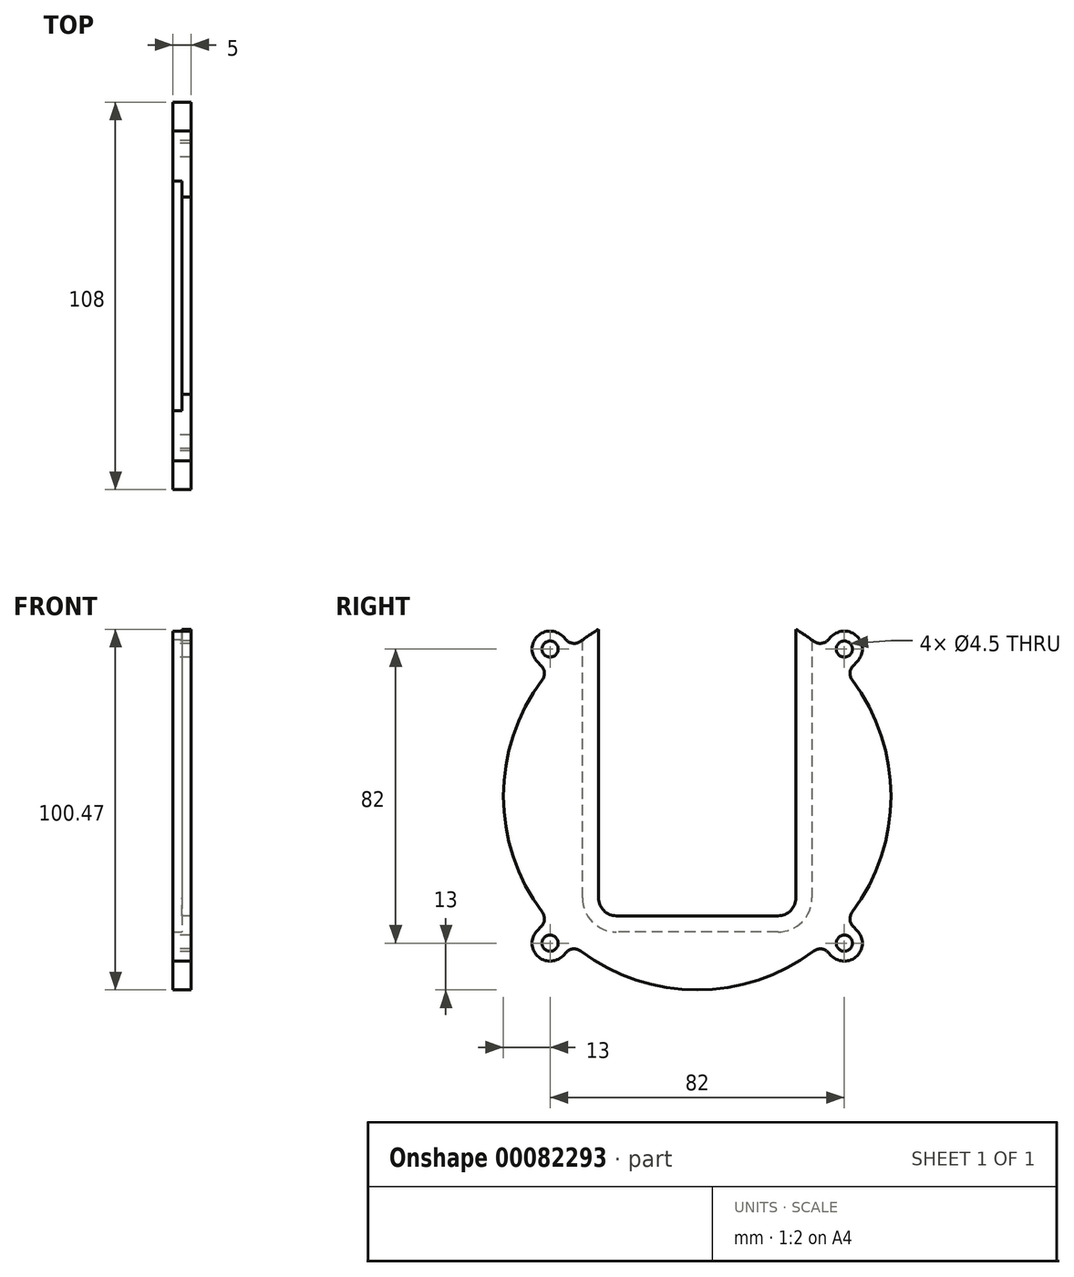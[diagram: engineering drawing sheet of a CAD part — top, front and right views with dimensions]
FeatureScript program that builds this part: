
annotation { "Feature Type Name" : "Feature", "Feature Type Description" : "" }
export const myFeature = defineFeature(function(context is Context, id is Id, definition is map)
    precondition{}
    {
        {
            var Q0;
            Q0=qCreatedBy(makeId("Right.planeOp"),FACE);
            var sketch = newSketch(context, id + "F0", { "sketchPlane" : qUnion([Q0])});
            skCircle(sketch, "E0", {"center": v(-41, 41) * mm, "radius": 2.25 * mm});
            skCircle(sketch, "E1", {"center": v(41, 41) * mm, "radius": 2.25 * mm});
            skCircle(sketch, "E2", {"center": v(41, -41) * mm, "radius": 2.25 * mm});
            skCircle(sketch, "E3", {"center": v(-41, -41) * mm, "radius": 2.25 * mm});
            skArc(sketch, "E4", {"start": v(-32.45, 43.16) * mm, "mid": v(-24.12, -48.31) * mm, "end": v(54, 0) * mm});
            skArc(sketch, "E5", {"start": v(37.46, -44.54) * mm, "mid": v(44.54, -44.54) * mm, "end": v(44.54, -37.46) * mm});
            skArc(sketch, "E6", {"start": v(-44.54, -37.46) * mm, "mid": v(-44.54, -44.54) * mm, "end": v(-37.46, -44.54) * mm});
            skLineSegment(sketch, "E7", {"start": v(-44.54, 37.46) * mm, "end": v(-36.42, 45.58) * mm, "construction": true});
            skLineSegment(sketch, "E8", {"start": v(-44.54, 37.46) * mm, "end": v(-43.44, 36.37) * mm});
            skLineSegment(sketch, "E9", {"start": v(-37.46, 44.54) * mm, "end": v(-36.37, 43.44) * mm});
            skLineSegment(sketch, "E10", {"start": v(37.46, 44.54) * mm, "end": v(46.12, 35.88) * mm, "construction": true});
            skLineSegment(sketch, "E11", {"start": v(37.46, 44.54) * mm, "end": v(36.37, 43.44) * mm});
            skLineSegment(sketch, "E12", {"start": v(44.54, 37.46) * mm, "end": v(43.44, 36.37) * mm});
            skLineSegment(sketch, "E13", {"start": v(-44.54, -37.46) * mm, "end": v(-35.54, -46.46) * mm, "construction": true});
            skLineSegment(sketch, "E14", {"start": v(-44.54, -37.46) * mm, "end": v(-43.44, -36.37) * mm});
            skLineSegment(sketch, "E15", {"start": v(-37.46, -44.54) * mm, "end": v(-36.37, -43.44) * mm});
            skLineSegment(sketch, "E16", {"start": v(37.46, -44.54) * mm, "end": v(47.36, -34.64) * mm, "construction": true});
            skLineSegment(sketch, "E17", {"start": v(37.46, -44.54) * mm, "end": v(36.37, -43.44) * mm});
            skLineSegment(sketch, "E18", {"start": v(44.54, -37.46) * mm, "end": v(43.44, -36.37) * mm});
            skArc(sketch, "E19.trimOffspring", {"start": v(-37.46, 44.54) * mm, "mid": v(-44.54, 44.54) * mm, "end": v(-44.54, 37.46) * mm});
            skArc(sketch, "E20.trimOffspring", {"start": v(32.45, 43.16) * mm, "mid": v(30.02, 44.89) * mm, "end": v(27.5, 46.47) * mm});
            skArc(sketch, "E21.trimOffspring", {"start": v(44.54, 37.46) * mm, "mid": v(44.54, 44.54) * mm, "end": v(37.46, 44.54) * mm});
            skArc(sketch, "E22.trimOffspring", {"start": v(-32.45, -43.16) * mm, "mid": v(0, -54) * mm, "end": v(32.45, -43.16) * mm});
            skPoint(sketch, "E23.visualSharp", {"position": v(-41.56, 34.48) * mm});
            skPoint(sketch, "E24.visualSharp", {"position": v(-34.48, 41.56) * mm});
            skArc(sketch, "E24.filletArc", {"start": v(-36.37, 43.44) * mm, "mid": v(-34.46, 42.57) * mm, "end": v(-32.45, 43.16) * mm});
            skPoint(sketch, "E25.visualSharp", {"position": v(-41.56, -34.48) * mm});
            skArc(sketch, "E25.filletArc", {"start": v(-43.44, -36.37) * mm, "mid": v(-42.57, -34.46) * mm, "end": v(-43.16, -32.45) * mm});
            skPoint(sketch, "E26.visualSharp", {"position": v(-34.48, -41.56) * mm});
            skArc(sketch, "E26.filletArc", {"start": v(-32.45, -43.16) * mm, "mid": v(-34.46, -42.57) * mm, "end": v(-36.37, -43.44) * mm});
            skPoint(sketch, "E27.visualSharp", {"position": v(41.56, -34.48) * mm});
            skArc(sketch, "E27.filletArc", {"start": v(43.16, -32.45) * mm, "mid": v(42.57, -34.46) * mm, "end": v(43.44, -36.37) * mm});
            skPoint(sketch, "E28.visualSharp", {"position": v(34.48, -41.56) * mm});
            skArc(sketch, "E28.filletArc", {"start": v(36.37, -43.44) * mm, "mid": v(34.46, -42.57) * mm, "end": v(32.45, -43.16) * mm});
            skPoint(sketch, "E29.visualSharp", {"position": v(41.56, 34.48) * mm});
            skArc(sketch, "E29.filletArc", {"start": v(43.44, 36.37) * mm, "mid": v(42.57, 34.46) * mm, "end": v(43.16, 32.45) * mm});
            skPoint(sketch, "E30.visualSharp", {"position": v(34.48, 41.56) * mm});
            skArc(sketch, "E30.filletArc", {"start": v(32.45, 43.16) * mm, "mid": v(34.46, 42.57) * mm, "end": v(36.37, 43.44) * mm});
            skArc(sketch, "E31.filletArc", {"start": v(-43.16, 32.45) * mm, "mid": v(-42.57, 34.46) * mm, "end": v(-43.44, 36.37) * mm});
            skArc(sketch, "E32.converted", {"start": v(-27.5, 46.47) * mm, "mid": v(0, -54) * mm, "end": v(27.5, 46.47) * mm});
            skLineSegment(sketch, "E33", {"start": v(-27.5, 46.47) * mm, "end": v(-27.5, -28.36) * mm});
            skLineSegment(sketch, "E34", {"start": v(27.5, 46.47) * mm, "end": v(27.5, -28.36) * mm});
            skLineSegment(sketch, "E35", {"start": v(-22.5, -33.36) * mm, "end": v(22.5, -33.36) * mm});
            skPoint(sketch, "E36.orphan", {"position": v(-27.5, -21.94) * mm});
            skPoint(sketch, "E37.orphan", {"position": v(27.5, -21.94) * mm});
            skPoint(sketch, "E38.visualSharp", {"position": v(-27.5, -33.36) * mm});
            skArc(sketch, "E38.filletArc", {"start": v(-27.5, -28.36) * mm, "mid": v(-26.04, -31.9) * mm, "end": v(-22.5, -33.36) * mm});
            skPoint(sketch, "E39.visualSharp", {"position": v(27.5, -33.36) * mm});
            skArc(sketch, "E39.filletArc", {"start": v(22.5, -33.36) * mm, "mid": v(26.04, -31.9) * mm, "end": v(27.5, -28.36) * mm});
            skArc(sketch, "E40.trimOffspring", {"start": v(-27.5, 46.47) * mm, "mid": v(-30.02, 44.89) * mm, "end": v(-32.45, 43.16) * mm});
            skPoint(sketch, "E41.orphan", {"position": v(-27.5, 53.27) * mm});
            skPoint(sketch, "E42.orphan", {"position": v(27.5, 53.27) * mm});
            skSolve(sketch);
        }
        {
            var Q0;
            Q0=qSketchRegion(id+"F0",true);
            extrude(context, id + "F1", {"entities" : qUnion([Q0]), "depth" : 5 * mm, "offsetDistance" : 25 * mm});
        }
        {
            var Q0;
            Q0=makeQuery(id+"F1.opExtrude","SWEPT_EDGE",EDGE,{"disambiguationData":[OSD([sQuery(id+"F0.wireOp",EDGE,"E32.converted"),sQuery(id+"F0.wireOp",EDGE,"E34")])]});
            cPoint(context, id + "F2", {"entities" : qUnion([Q0]), "parameter" : 0.5});
        }
        {
            var Q0;
            Q0=qCreatedBy(makeId("Top.planeOp"),FACE);
            var Q1;
            Q1=qCreatedBy(id+"F2",VERTEX);
            cPlane(context, id + "F3", {"entities" : qUnion([Q0, Q1]), "cplaneType" : CPlaneType.PLANE_POINT, "offset" : 30.6 * mm, "width" : 150 * mm, "height" : 150 * mm});
        }
        {
            var Q0;
            Q0=qCreatedBy(id+"F3.planeOp",FACE);
            var sketch = newSketch(context, id + "F4", { "sketchPlane" : qUnion([Q0])});
            skLineSegment(sketch, "E43", {"start": v(0, 26.5) * mm, "end": v(0, 32) * mm});
            skLineSegment(sketch, "E44", {"start": v(0, 32) * mm, "end": v(2.5, 32) * mm});
            skLineSegment(sketch, "E45", {"start": v(2.5, 32) * mm, "end": v(2.5, 26.5) * mm});
            skLineSegment(sketch, "E46", {"start": v(2.5, 26.5) * mm, "end": v(0, 26.5) * mm});
            skSolve(sketch);
        }
        {
            var Q0;
            Q0=makeQuery(id+"F4.imprint","IMPRINT",FACE,{"disambiguationData":[TD([[makeQuery(id+"F4.imprint","IMPRINT",EDGE,{"derivedFrom":sQuery(id+"F4.wireOp",EDGE,"E43")}),-1.0]])]});
            var Q1;
            Q1=makeQuery(id+"F1.opExtrude","CAP_EDGE",EDGE,{"disambiguationData":[OSD([sQuery(id+"F0.wireOp",EDGE,"E34")])],"isStart":false});
            var Q2;
            Q2=makeQuery(id+"F1.opExtrude","CAP_EDGE",EDGE,{"disambiguationData":[OSD([sQuery(id+"F0.wireOp",EDGE,"E39.filletArc")])],"isStart":false});
            var Q3;
            Q3=makeQuery(id+"F1.opExtrude","CAP_EDGE",EDGE,{"disambiguationData":[OSD([sQuery(id+"F0.wireOp",EDGE,"E35")])],"isStart":false});
            var Q4;
            Q4=makeQuery(id+"F1.opExtrude","CAP_EDGE",EDGE,{"disambiguationData":[OSD([sQuery(id+"F0.wireOp",EDGE,"E38.filletArc")])],"isStart":false});
            var Q5;
            Q5=makeQuery(id+"F1.opExtrude","CAP_EDGE",EDGE,{"disambiguationData":[OSD([sQuery(id+"F0.wireOp",EDGE,"E33")])],"isStart":false});
            sweep(context, id + "F5", {"operationType" : NewBodyOperationType.REMOVE, "profiles" : qUnion([Q0]), "path" : qUnion([Q1, Q2, Q3, Q4, Q5])});
        }
    });
